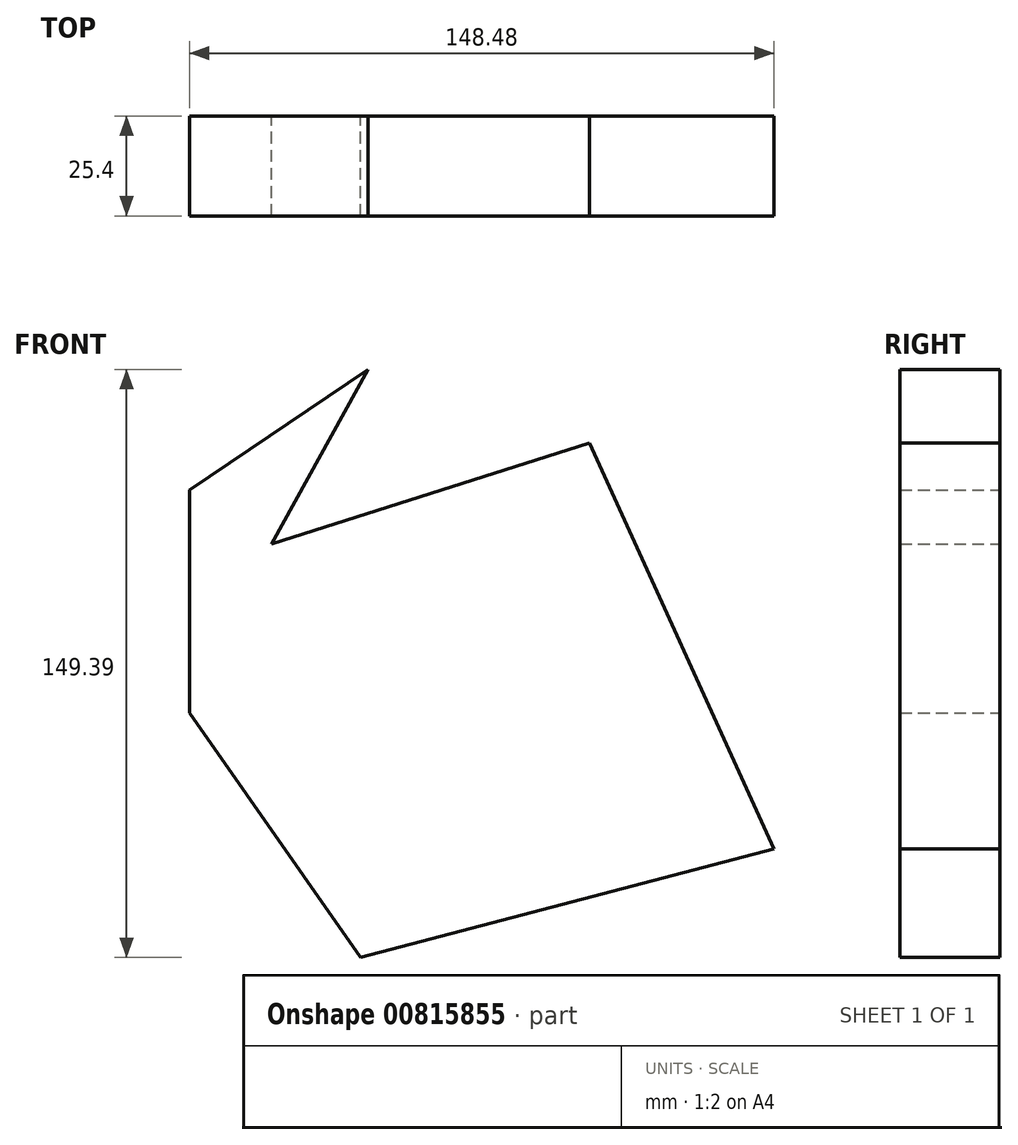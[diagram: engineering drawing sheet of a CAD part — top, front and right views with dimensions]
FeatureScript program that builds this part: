
annotation { "Feature Type Name" : "Feature", "Feature Type Description" : "" }
export const myFeature = defineFeature(function(context is Context, id is Id, definition is map)
    precondition{}
    {
        {
            var Q0;
            Q0=qCreatedBy(makeId("Front.planeOp"),FACE);
            var sketch = newSketch(context, id + "F0", { "sketchPlane" : qUnion([Q0])});
            skLineSegment(sketch, "E0", {"start": v(0, 0) * mm, "end": v(0, 56.7) * mm});
            skLineSegment(sketch, "E1", {"start": v(0, 56.7) * mm, "end": v(45.3, 87.31) * mm});
            skLineSegment(sketch, "E2", {"start": v(45.3, 87.31) * mm, "end": v(20.82, 42.92) * mm});
            skLineSegment(sketch, "E3", {"start": v(20.82, 42.92) * mm, "end": v(101.64, 68.64) * mm});
            skLineSegment(sketch, "E4", {"start": v(101.64, 68.64) * mm, "end": v(148.48, -34.53) * mm});
            skLineSegment(sketch, "E5", {"start": v(148.48, -34.53) * mm, "end": v(43.47, -62.08) * mm});
            skLineSegment(sketch, "E6", {"start": v(43.47, -62.08) * mm, "end": v(0, 0) * mm});
            skSolve(sketch);
        }
        {
            var Q0;
            Q0=makeQuery(id+"F0.imprint","IMPRINT",FACE,{"disambiguationData":[TD([[makeQuery(id+"F0.imprint","IMPRINT",EDGE,{"derivedFrom":sQuery(id+"F0.wireOp",EDGE,"E0")}),-1.0]])]});
            extrude(context, id + "F1", {"entities" : qUnion([Q0]), "depth" : 25.4 * mm, "offsetDistance" : 25.4 * mm});
        }
    });
